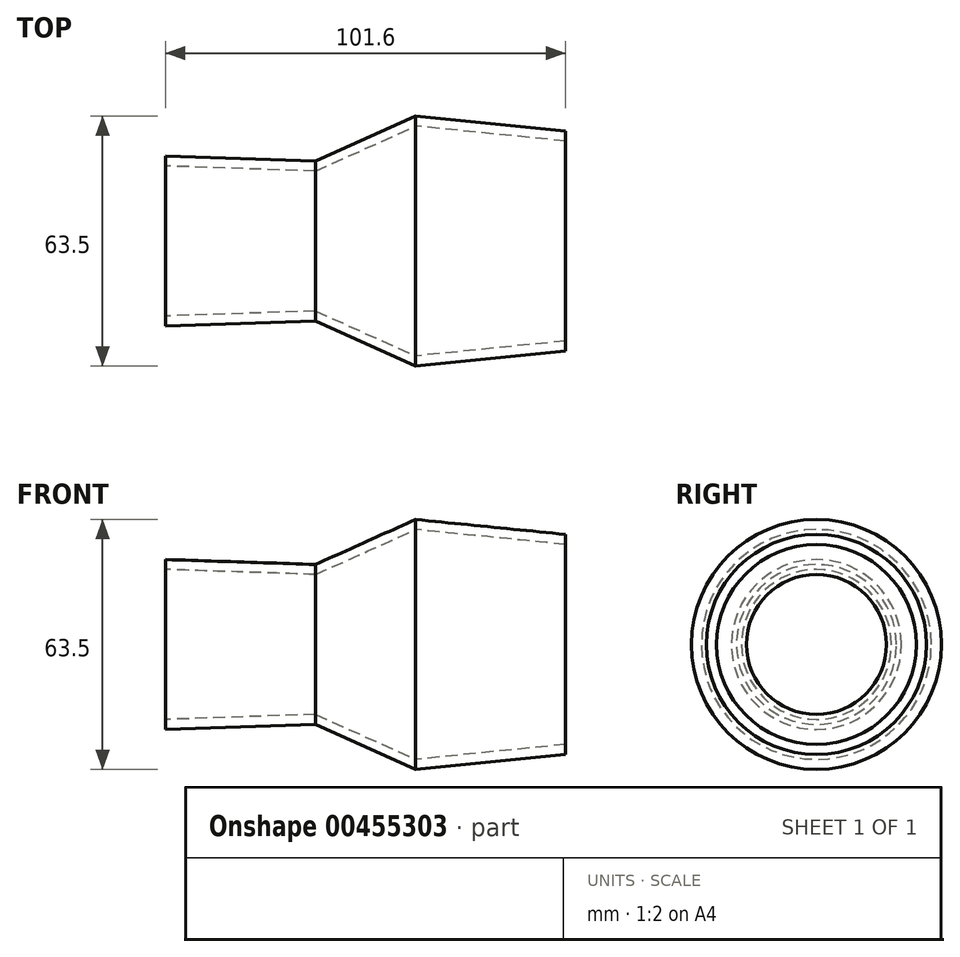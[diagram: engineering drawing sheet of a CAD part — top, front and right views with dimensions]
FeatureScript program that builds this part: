
annotation { "Feature Type Name" : "Feature", "Feature Type Description" : "" }
export const myFeature = defineFeature(function(context is Context, id is Id, definition is map)
    precondition{}
    {
        {
            var Q0;
            Q0=qCreatedBy(makeId("Front.planeOp"),FACE);
            var sketch = newSketch(context, id + "F0", { "sketchPlane" : qUnion([Q0])});
            skLineSegment(sketch, "E0", {"start": v(-50.8, 19.05) * mm, "end": v(-12.7, 17.78) * mm});
            skLineSegment(sketch, "E1", {"start": v(12.7, 31.75) * mm, "end": v(50.8, 27.95) * mm});
            skLineSegment(sketch, "E2.1", {"start": v(12.7, 29.2) * mm, "end": v(50.8, 25.4) * mm});
            skLineSegment(sketch, "E3.0", {"start": v(-50.8, 21.6) * mm, "end": v(-12.7, 20.32) * mm});
            skLineSegment(sketch, "E4", {"start": v(-12.7, 20.32) * mm, "end": v(12.7, 31.75) * mm});
            skLineSegment(sketch, "E5", {"start": v(-12.7, 17.78) * mm, "end": v(12.7, 29.2) * mm});
            skLineSegment(sketch, "E6", {"start": v(-50.8, 21.6) * mm, "end": v(-50.8, 19.05) * mm});
            skLineSegment(sketch, "E7", {"start": v(50.8, 25.4) * mm, "end": v(50.8, 27.95) * mm});
            skLineSegment(sketch, "E8", {"start": v(-50.8, 0) * mm, "end": v(50.8, 0) * mm});
            skPoint(sketch, "E9", {"position": v(0, 0) * mm});
            skSolve(sketch);
        }
        {
            var Q0;
            Q0=makeQuery(id+"F0.imprint","IMPRINT",FACE,{"disambiguationData":[TD([[makeQuery(id+"F0.imprint","IMPRINT",EDGE,{"derivedFrom":sQuery(id+"F0.wireOp",EDGE,"E0")}),1.0]])]});
            var Q1;
            Q1=sQuery(id+"F0.wireOp",EDGE,"E8");
            revolve(context, id + "F1", {"entities" : qUnion([Q0]), "axis" : qUnion([Q1]), "revolveType" : RevolveType.FULL});
        }
    });
